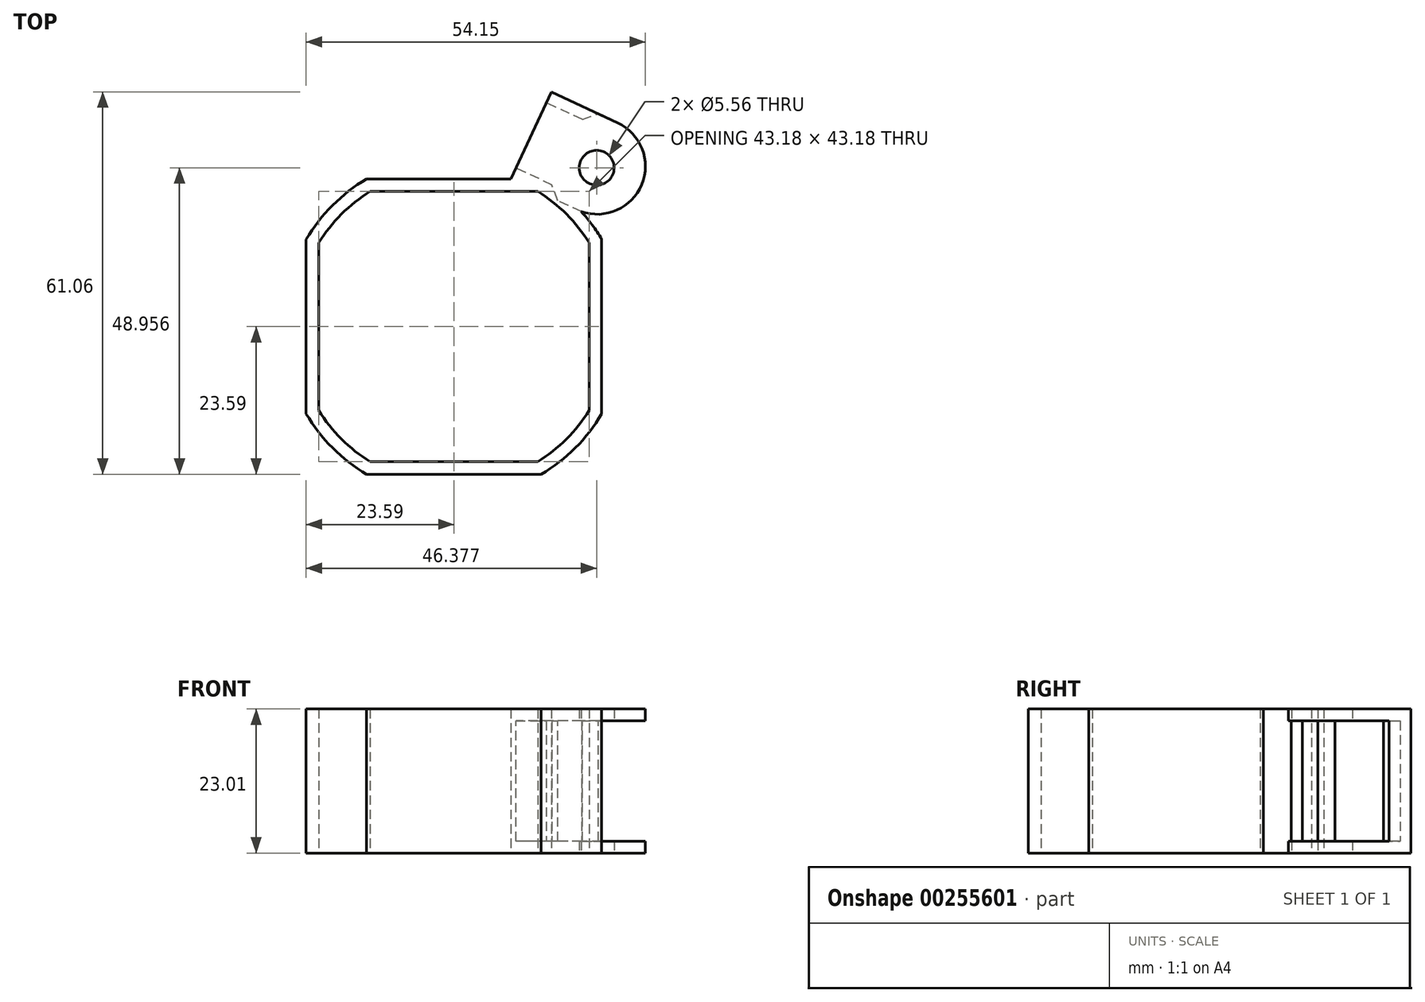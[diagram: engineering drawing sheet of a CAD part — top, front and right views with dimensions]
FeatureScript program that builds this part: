
annotation { "Feature Type Name" : "Feature", "Feature Type Description" : "" }
export const myFeature = defineFeature(function(context is Context, id is Id, definition is map)
    precondition{}
    {
        {
            var Q0;
            Q0=qCreatedBy(makeId("Top.planeOp"),FACE);
            var sketch = newSketch(context, id + "F0", { "sketchPlane" : qUnion([Q0])});
            skLineSegment(sketch, "E0.bottom", {"start": v(13.23, 21.08) * mm, "end": v(-13.23, 21.08) * mm, "construction": true});
            skLineSegment(sketch, "E0.top", {"start": v(13.23, -21.08) * mm, "end": v(-13.23, -21.08) * mm, "construction": true});
            skLineSegment(sketch, "E0.left", {"start": v(21.08, 13.23) * mm, "end": v(21.08, -13.23) * mm, "construction": true});
            skLineSegment(sketch, "E0.right", {"start": v(-21.08, 13.23) * mm, "end": v(-21.08, -13.23) * mm, "construction": true});
            skPoint(sketch, "E0.middle", {"position": v(0, 0) * mm});
            skArc(sketch, "E1", {"start": v(-21.08, -13.23) * mm, "mid": v(-17.6, -17.6) * mm, "end": v(-13.23, -21.08) * mm, "construction": true});
            skPoint(sketch, "E2.orphan", {"position": v(-21.08, 21.08) * mm});
            skArc(sketch, "E3.trimOffspring", {"start": v(13.23, -21.08) * mm, "mid": v(17.6, -17.6) * mm, "end": v(21.08, -13.23) * mm, "construction": true});
            skPoint(sketch, "E4.orphan", {"position": v(-21.08, -21.08) * mm});
            skPoint(sketch, "E5.orphan", {"position": v(21.08, -21.08) * mm});
            skArc(sketch, "E6.trimOffspring", {"start": v(21.08, 13.23) * mm, "mid": v(17.6, 17.6) * mm, "end": v(13.23, 21.08) * mm, "construction": true});
            skPoint(sketch, "E7.orphan", {"position": v(21.08, 21.08) * mm});
            skArc(sketch, "E8.trimOffspring", {"start": v(-13.23, 21.08) * mm, "mid": v(-17.6, 17.6) * mm, "end": v(-21.08, 13.23) * mm, "construction": true});
            skArc(sketch, "E9.0", {"start": v(21.59, 13.38) * mm, "mid": v(17.96, 17.96) * mm, "end": v(13.38, 21.59) * mm});
            skLineSegment(sketch, "E9.1", {"start": v(13.38, 21.59) * mm, "end": v(-13.38, 21.59) * mm});
            skLineSegment(sketch, "E9.2", {"start": v(21.59, 13.38) * mm, "end": v(21.59, -13.38) * mm});
            skArc(sketch, "E9.3", {"start": v(-13.38, 21.59) * mm, "mid": v(-17.96, 17.96) * mm, "end": v(-21.59, 13.38) * mm});
            skArc(sketch, "E9.4", {"start": v(13.38, -21.59) * mm, "mid": v(17.96, -17.96) * mm, "end": v(21.6, -13.38) * mm});
            skLineSegment(sketch, "E9.5", {"start": v(13.38, -21.59) * mm, "end": v(-13.38, -21.59) * mm});
            skArc(sketch, "E9.6", {"start": v(-21.59, -13.38) * mm, "mid": v(-17.96, -17.96) * mm, "end": v(-13.38, -21.59) * mm});
            skLineSegment(sketch, "E9.7", {"start": v(-21.59, 13.38) * mm, "end": v(-21.59, -13.38) * mm});
            skLineSegment(sketch, "E10.0", {"start": v(13.94, -23.59) * mm, "end": v(-13.94, -23.59) * mm});
            skArc(sketch, "E10.1", {"start": v(-23.59, -13.94) * mm, "mid": v(-19.37, -19.37) * mm, "end": v(-13.94, -23.6) * mm});
            skArc(sketch, "E10.2", {"start": v(13.94, -23.6) * mm, "mid": v(19.37, -19.37) * mm, "end": v(23.6, -13.94) * mm});
            skLineSegment(sketch, "E10.3", {"start": v(-23.59, 13.94) * mm, "end": v(-23.59, -13.94) * mm});
            skLineSegment(sketch, "E10.4", {"start": v(23.59, 13.94) * mm, "end": v(23.59, -13.94) * mm});
            skArc(sketch, "E10.5", {"start": v(23.6, 13.94) * mm, "mid": v(19.37, 19.37) * mm, "end": v(13.94, 23.6) * mm});
            skLineSegment(sketch, "E10.6", {"start": v(13.94, 23.59) * mm, "end": v(-13.94, 23.59) * mm});
            skArc(sketch, "E10.7", {"start": v(-13.94, 23.6) * mm, "mid": v(-19.37, 19.37) * mm, "end": v(-23.59, 13.94) * mm});
            skSolve(sketch);
        }
        {
            var Q0;
            Q0=makeQuery(id+"F0.imprint","IMPRINT",FACE,{"disambiguationData":[TD([[makeQuery(id+"F0.imprint","IMPRINT",EDGE,{"derivedFrom":sQuery(id+"F0.wireOp",EDGE,"E0.bottom")}),-1.0]])]});
            var Q1;
            Q1=makeQuery(id+"F0.imprint","IMPRINT",FACE,{"disambiguationData":[TD([[makeQuery(id+"F0.imprint","IMPRINT",EDGE,{"derivedFrom":sQuery(id+"F0.wireOp",EDGE,"E9.0")}),-1.0]])]});
            extrude(context, id + "F1", {"entities" : qUnion([Q0, Q1]), "depth" : 23.01 * mm});
        }
        {
            var Q0;
            Q0=qCreatedBy(makeId("Top.planeOp"),FACE);
            var sketch = newSketch(context, id + "F2", { "sketchPlane" : qUnion([Q0])});
            skLineSegment(sketch, "E11", {"start": v(9.1, 23.6) * mm, "end": v(19.66, 18.66) * mm});
            skLineSegment(sketch, "E12", {"start": v(9.1, 23.59) * mm, "end": v(15.56, 37.47) * mm});
            skLineSegment(sketch, "E13", {"start": v(15.56, 37.47) * mm, "end": v(26.13, 32.54) * mm});
            skCircle(sketch, "E14", {"center": v(22.79, 25.37) * mm, "radius": 2.78 * mm});
            skLineSegment(sketch, "E15.0", {"start": v(23.59, 13.94) * mm, "end": v(23.59, -13.94) * mm});
            skPoint(sketch, "E16.orphan", {"position": v(13.94, 23.59) * mm});
            skArc(sketch, "E17.trimOffspring", {"start": v(19.66, 18.66) * mm, "mid": v(29.84, 22.37) * mm, "end": v(26.13, 32.54) * mm});
            skSolve(sketch);
        }
        {
            var Q0;
            Q0=makeQuery(id+"F2.imprint","IMPRINT",FACE,{"disambiguationData":[TD([[makeQuery(id+"F2.imprint","IMPRINT",EDGE,{"derivedFrom":sQuery(id+"F2.wireOp",EDGE,"E11")}),1.0]])]});
            var Q1;
            Q1=makeQuery(id+"F1.opExtrude","CAP_FACE",FACE,{"disambiguationData":[OSD([sQuery(id+"F0.wireOp",EDGE,"E9.0"),sQuery(id+"F0.wireOp",EDGE,"E9.1"),sQuery(id+"F0.wireOp",EDGE,"E9.2"),sQuery(id+"F0.wireOp",EDGE,"E9.3"),sQuery(id+"F0.wireOp",EDGE,"E9.4"),sQuery(id+"F0.wireOp",EDGE,"E9.5"),sQuery(id+"F0.wireOp",EDGE,"E9.6"),sQuery(id+"F0.wireOp",EDGE,"E9.7"),sQuery(id+"F0.wireOp",EDGE,"E10.0"),sQuery(id+"F0.wireOp",EDGE,"E10.1"),sQuery(id+"F0.wireOp",EDGE,"E10.2"),sQuery(id+"F0.wireOp",EDGE,"E10.3"),sQuery(id+"F0.wireOp",EDGE,"E10.4"),sQuery(id+"F0.wireOp",EDGE,"E10.5"),sQuery(id+"F0.wireOp",EDGE,"E10.6"),sQuery(id+"F0.wireOp",EDGE,"E10.7")])],"isStart":false});
            extrude(context, id + "F3", {"entities" : qUnion([Q0]), "operationType" : NewBodyOperationType.ADD, "endBound" : BoundingType.UP_TO_SURFACE, "endBoundEntityFace" : qUnion([Q1]), "depth" : 25.4 * mm});
        }
        {
            var Q0;
            Q0=makeQuery(id+"F3.opExtrude","SWEPT_FACE",FACE,{"disambiguationData":[OSD([sQuery(id+"F2.wireOp",EDGE,"E12")])]});
            var sketch = newSketch(context, id + "F4", { "sketchPlane" : qUnion([Q0])});
            skLineSegment(sketch, "E18.0", {"start": v(-27.13, 1.9) * mm, "end": v(-27.13, 21.1) * mm});
            skLineSegment(sketch, "E18.1", {"start": v(-38.63, 1.9) * mm, "end": v(-27.13, 1.9) * mm});
            skLineSegment(sketch, "E18.2", {"start": v(-38.63, 21.1) * mm, "end": v(-38.63, 1.9) * mm});
            skLineSegment(sketch, "E18.3", {"start": v(-27.13, 21.1) * mm, "end": v(-38.63, 21.1) * mm});
            skSolve(sketch);
        }
        {
            var Q0;
            Q0=makeQuery(id+"F4.imprint","IMPRINT",FACE,{"disambiguationData":[TD([[makeQuery(id+"F4.imprint","IMPRINT",EDGE,{"derivedFrom":sQuery(id+"F4.wireOp",EDGE,"E18.0")}),1.0]])]});
            extrude(context, id + "F5", {"entities" : qUnion([Q0]), "operationType" : NewBodyOperationType.REMOVE, "endBound" : BoundingType.THROUGH_ALL, "oppositeDirection" : true, "depth" : 25.4 * mm});
        }
        {
            var Q0;
            Q0=makeQuery(id+"F3.opExtrude","SWEPT_FACE",FACE,{"disambiguationData":[OSD([sQuery(id+"F2.wireOp",EDGE,"E13")])]});
            var sketch = newSketch(context, id + "F6", { "sketchPlane" : qUnion([Q0])});
            skLineSegment(sketch, "E19.bottom", {"start": v(-17.6, 1.9) * mm, "end": v(-6.52, 1.9) * mm});
            skLineSegment(sketch, "E19.top", {"start": v(-17.6, 21.1) * mm, "end": v(-6.52, 21.1) * mm});
            skLineSegment(sketch, "E19.left", {"start": v(-17.6, 1.9) * mm, "end": v(-17.6, 21.1) * mm});
            skLineSegment(sketch, "E19.right", {"start": v(-6.52, 1.9) * mm, "end": v(-6.52, 21.1) * mm});
            skSolve(sketch);
        }
        {
            var Q0;
            Q0 = qSketchRegion(id + "F6", true);
            var Q1;
            Q1=makeQuery(id+"F3.opExtrude","SWEPT_FACE",FACE,{"disambiguationData":[OSD([sQuery(id+"F2.wireOp",EDGE,"E11")])]});
            extrude(context, id + "F7", {"entities" : qUnion([Q0]), "operationType" : NewBodyOperationType.REMOVE, "oppositeDirection" : true, "endBoundEntityFace" : qUnion([Q1]), "depth" : 15.32 * mm});
        }
        {
            var Q0;
            Q0=makeQuery(id+"F7.boolean.opBoolean","INTERSECT",EDGE,{"derivedFrom":[makeQuery(id+"F5.boolean.opBoolean","COPY",FACE,{"derivedFrom":makeQuery(id+"F5.opExtrude","SWEPT_FACE",FACE,{"disambiguationData":[OSD([sQuery(id+"F4.wireOp",EDGE,"E18.0")])]})}),makeQuery(id+"F7.opExtrude","SWEPT_FACE",FACE,{"disambiguationData":[OSD([sQuery(id+"F6.wireOp",EDGE,"E19.right")])]})]});
            var Q1;
            Q1=makeQuery(id+"F7.boolean.opBoolean","INTERSECT",EDGE,{"derivedFrom":[makeQuery(id+"F5.boolean.opBoolean","COPY",FACE,{"derivedFrom":makeQuery(id+"F5.opExtrude","SWEPT_FACE",FACE,{"disambiguationData":[OSD([sQuery(id+"F4.wireOp",EDGE,"E18.2")])]})}),makeQuery(id+"F7.opExtrude","SWEPT_FACE",FACE,{"disambiguationData":[OSD([sQuery(id+"F6.wireOp",EDGE,"E19.right")])]})]});
            chamfer(context, id + "F8", {"entities" : qUnion([Q0, Q1]), "width" : 1.9 * mm, "tangentPropagation" : true});
        }
    });
